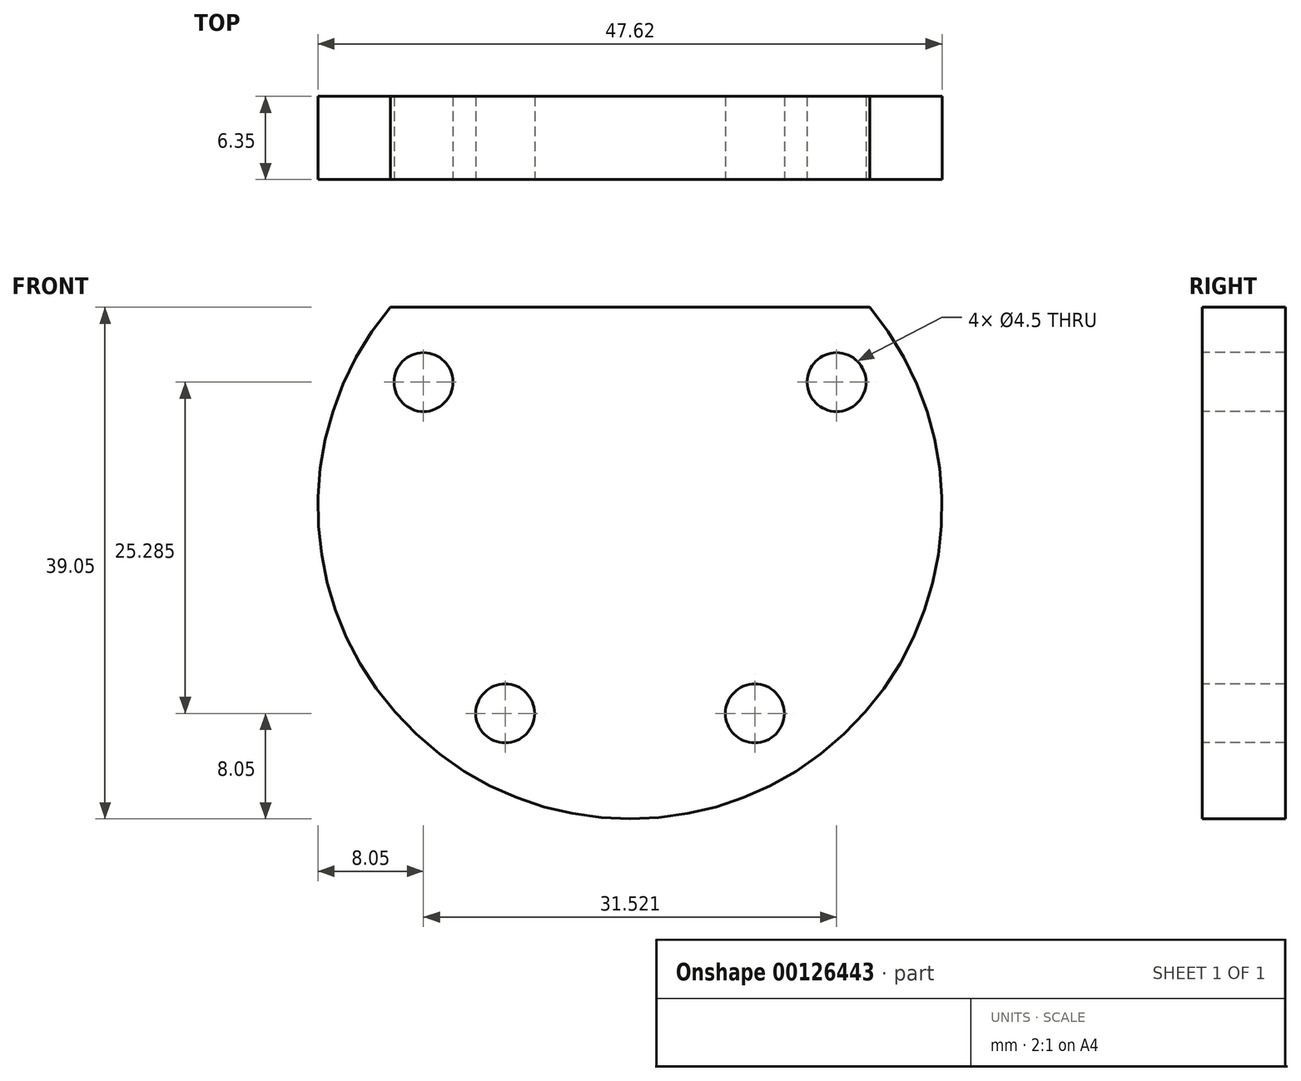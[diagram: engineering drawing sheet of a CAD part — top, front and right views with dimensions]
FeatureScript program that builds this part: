
annotation { "Feature Type Name" : "Feature", "Feature Type Description" : "" }
export const myFeature = defineFeature(function(context is Context, id is Id, definition is map)
    precondition{}
    {
        {
            var Q0;
            Q0=qCreatedBy(makeId("Front.planeOp"),FACE);
            var sketch = newSketch(context, id + "F0", { "sketchPlane" : qUnion([Q0])});
            skArc(sketch, "E0", {"start": v(-18.3, 15.24) * mm, "mid": v(0, -23.81) * mm, "end": v(18.3, 15.24) * mm});
            skLineSegment(sketch, "E1", {"start": v(-18.3, 15.24) * mm, "end": v(18.3, 15.24) * mm});
            skLineSegment(sketch, "E2", {"start": v(18.3, 15.24) * mm, "end": v(18.3, 15.24) * mm});
            skSolve(sketch);
        }
        {
            var Q0;
            Q0 = qSketchRegion(id + "F0", true);
            extrude(context, id + "F1", {"entities" : qUnion([Q0]), "depth" : 6.35 * mm});
        }
        {
            var Q0;
            Q0=makeQuery(id+"F1.opExtrude","CAP_FACE",FACE,{"disambiguationData":[OSD([sQuery(id+"F0.wireOp",EDGE,"E0"),sQuery(id+"F0.wireOp",EDGE,"E1")])],"isStart":false});
            var sketch = newSketch(context, id + "F2", { "sketchPlane" : qUnion([Q0])});
            skCircle(sketch, "E3", {"center": v(0, 0) * mm, "radius": 18.41 * mm});
            skPoint(sketch, "E4", {"position": v(-15.76, 9.53) * mm});
            skPoint(sketch, "E5", {"position": v(-9.53, -15.76) * mm});
            skPoint(sketch, "E6", {"position": v(9.53, -15.76) * mm});
            skPoint(sketch, "E7", {"position": v(15.76, 9.53) * mm});
            skSolve(sketch);
        }
        {
            var Q0;
            Q0=sQuery(id+"F2.wireOp",VERTEX,"E4");
            var Q1;
            Q1=sQuery(id+"F2.wireOp",VERTEX,"E7");
            var Q2;
            Q2=sQuery(id+"F2.wireOp",VERTEX,"E5");
            var Q3;
            Q3=sQuery(id+"F2.wireOp",VERTEX,"E6");
            var Q4;
            Q4=makeQuery(id+"F1.opExtrude","SWEPT_BODY",BODY,{"disambiguationData":[OSD([sQuery(id+"F0.wireOp",EDGE,"E0"),sQuery(id+"F0.wireOp",EDGE,"E1")])]});
            hole(context, id + "F3", {"style" : HoleStyle.SIMPLE, "endStyle" : HoleEndStyle.THROUGH, "standardTappedOrClearance" : lookupTablePath({ "standard" : "ANSI", "fit" : "Normal (ASME)", "size" : "#8", "type" : "Clearance" }), "standardBlindInLast" : lookupTablePath({ "fit" : "Free", "standard" : "ANSI", "size" : "#8", "type" : "Clearance" }), "holeDiameter" : 4.5 * mm, "locations" : qUnion([Q0, Q1, Q2, Q3]), "scope" : qUnion([Q4]), "isTappedThrough" : true});
        }
    });
